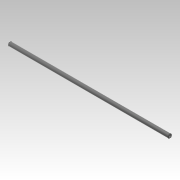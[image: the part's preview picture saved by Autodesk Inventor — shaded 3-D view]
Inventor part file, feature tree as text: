
AUTODESK INVENTOR PART (.ipt)
format: ipt  version: 2020 (Build 240168000, 168)  size: 86,016 bytes
history: native  units: mm
features: revolve x1, chamfer x1, sketch x1
ambient origin geometry x8: Origin, YZ Plane, XZ Plane, XY Plane, X Axis, Y Axis, Z Axis, Center Point
bodies: Solid1 (feature_tree)
feature tree (3):
  revolve  "Revolution1"  [1 undecoded]
  chamfer  "Chamfer1"  Distance=250.0mm
  sketch  "Sketch1"  dims[d0=2.0mm d1=3.0mm d2=250.0mm d3=90.0deg d4=0.5mm d5=2.0mm d6=45.0deg]
note: 1 required parameter value undecoded (feature->parameter linkage not recoverable at this tier; creation-order binding heuristic only, values carry confidence <= 0.55)
